# Revit family: Hanger_No10_EMCO
name_source: partatom
category: Generic Models
units: mm (PartAtom-declared; Revit-internal decimal feet)

## family parameters
Always vertical = Yes
Can host rebar = No
Cut with Voids When Loaded = No
Maintain Annotation Orientation = No
Part Type = Normal
Room Calculation Point = No
Round Connector Dimension = Use Diameter
Shared = No
Work Plane-Based = Yes

## types (3) — shared parameters
Assembly Code = E1090900
Construction Details = http://emcospi.com
Default Elevation = 4' - 0"
Hanger Material = EMCO  - Dark Brown Molded Plastic
Installation Phase = Closet and Utiity Shelving Hardware
Installation-Fabrication = http://emcospi.com
Keynote = 10 57 33
Manufacturer = EMCO Specialty Products, Inc.
Manufacturer Fax = 913-281-4554
Manufacturer Website = http://www.emcospi.com
Product Data = http://emcospi.com
Product Properties = http://www.arcat.com
Sales Information = http://www.emcospi.com
Send Message = http://www.emcospi.com
URL = https://www.arcat.com
Warranty Duration (Years) = 1
zero-valued in all types: Expected Lifespan (Years)

## per-type parameters (varying)
| type | A receptacle | Ball Top | C Receptacle | Hook Material | Open Hook |
| EMCO_No. 10 Hanger- Open Hook | No | No | No | EMCO  - Heavy Guage Plated Steel | Yes |
| EMCO_No. 10 Hanger - Ball Top w/ "A" Receptacle | Yes | Yes | No | <By Category> | No |
| EMCO_No. 10 Hanger - Ball Top w/ "C" Receptacle | No | Yes | Yes | <By Category> | No |

note: column(s) folded — value = type name in every type: Description, Model

## geometry (parser evidence)
native form markers: Sweep x6
no freeform markers — native parametric forms only
